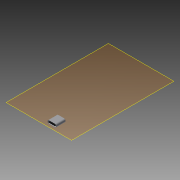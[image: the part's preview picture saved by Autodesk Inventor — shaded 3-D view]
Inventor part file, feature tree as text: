
AUTODESK INVENTOR PART (.ipt)
format: ipt  version: 2013 SP2 (Build 170200200, 200)  size: 125,952 bytes
history: native  units: mm
features: extrude x2, sketch x2, plane x1, fillet x1, shell x1
ambient origin geometry x8: Origin, YZ Plane, XZ Plane, XY Plane, X Axis, Y Axis, Z Axis, Center Point
bodies: Solid1 (feature_tree)
feature tree (7):
  plane  "Work Plane1"
  extrude  "Extrusion1"  Depth=10.0mm
  fillet  "Fillet1"  Radius=3.5mm
  shell  "Shell1"  Thickness=1.5mm
  extrude  "Extrusion2"  Depth=1.0mm
  sketch  "Sketch1"  dims[d0=9.3mm d2=10.0mm d3=3.5mm d4=0.0mm d5=1.5mm]
  sketch  "Sketch2"  dims[d6=0.2mm d7=1.0mm d9=3.5mm d10=0.0mm]
